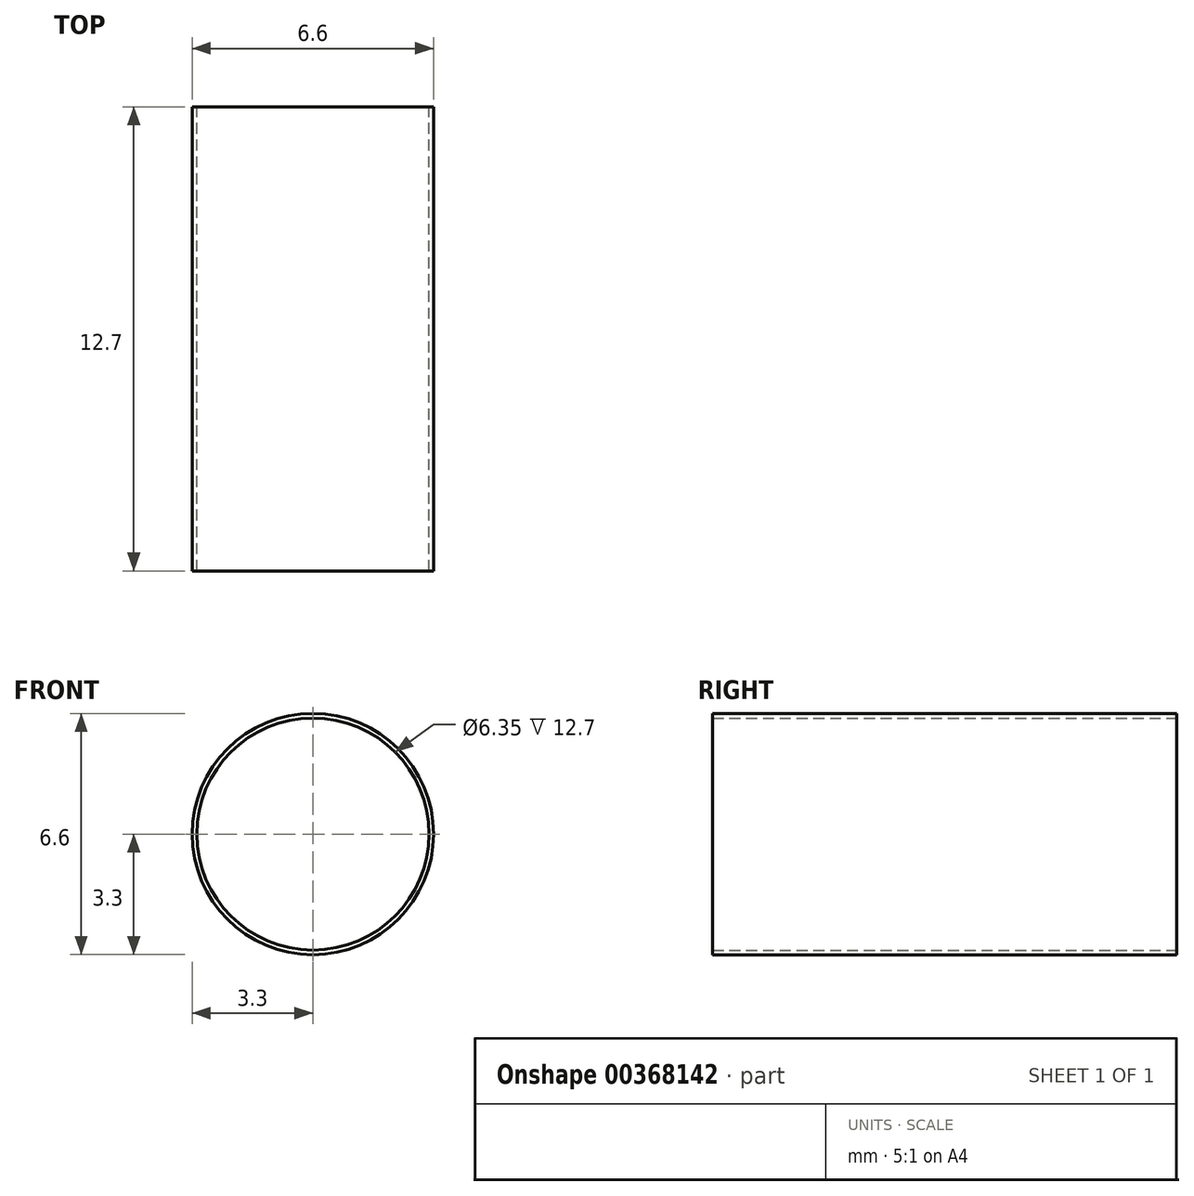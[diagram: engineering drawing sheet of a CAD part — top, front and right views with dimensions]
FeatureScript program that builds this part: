
annotation { "Feature Type Name" : "Feature", "Feature Type Description" : "" }
export const myFeature = defineFeature(function(context is Context, id is Id, definition is map)
    precondition{}
    {
        {
            var Q0;
            Q0=qCreatedBy(makeId("Front.planeOp"),FACE);
            var sketch = newSketch(context, id + "F0", { "sketchPlane" : qUnion([Q0])});
            skCircle(sketch, "E0", {"center": v(0, 0) * mm, "radius": 3.3 * mm});
            skCircle(sketch, "E1", {"center": v(0, 0) * mm, "radius": 3.18 * mm});
            skSolve(sketch);
        }
        {
            var Q0;
            Q0=makeQuery(id+"F0.imprint","IMPRINT",FACE,{"disambiguationData":[TD([[makeQuery(id+"F0.imprint","IMPRINT",EDGE,{"derivedFrom":sQuery(id+"F0.wireOp",EDGE,"E0")}),1.0]])]});
            extrude(context, id + "F1", {"entities" : qUnion([Q0]), "depth" : 12.7 * mm, "offsetDistance" : 25.4 * mm});
        }
    });
